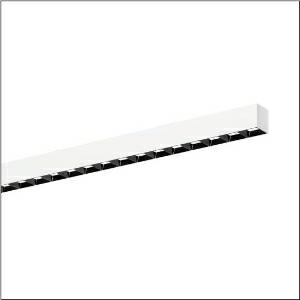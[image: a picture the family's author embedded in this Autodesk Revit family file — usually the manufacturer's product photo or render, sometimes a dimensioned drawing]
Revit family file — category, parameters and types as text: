
# Revit family: silica_r__21_51mx22tat4w_9510
name_source: partatom
category: Lighting Fixtures
units: mm (PartAtom-declared; Revit-internal decimal feet)

## family parameters
Cut with Voids When Loaded = No
Host = Face
Light Source = No
Part Type = Normal
Room Calculation Point = No
Round Connector Dimension = Use Diameter
Shared = No

## types (1)
- --- (1 x LED, 3720 lm, 32.1 W, 6500K)
    Apparent Load = 32 VA
    CIE Flux Codes = 84 100 100 100 100
    Color Rendering = 80
    Color Temperature = 6500K
    Default Elevation = 1800 mm
    Description = Silica® 21, office luminaire, primary light control with darklight reflector, of PMMA, black, CAT 2 (L<= 3000cd/m²), light emission: direct distribution, primary light characteristic: symmetric, installation type: surface-mounted, LED, rated luminous flux: 3.720lm, luminous efficacy: 110lm/W, light colour: 8tw, colour temperature: 2700..6500K, control gear: DALI DT8, with terminal, 3+2-pole, max. 2.5mm², mains connection: 220..240V, AC, 50/60Hz, rated input power: 33.8W, luminaire housing, of aluminium, traffic white (RAL 9016), length: 1.204mm, width: 53mm, height: 53mm, protection rating (complete): IP20, insulation class (complete): insulation class I (protective earthing), certification: CE, permissible operating ambient temperature: 0..+35°C, standard: EN 50419, packaging unit: 1 piece
    Height = 53 mm
    Lamp = 1 x LED
    Lamp Light Flux = 3720 lm
    Lamp Power = 32.1 W
    Lamp count = 1
    Length = 1204 mm
    Luminous efficacy = 116 lm/W
    Manufacturer = Siteco
    ModVariant = No
    Model = 51MX22TAT4W
    Mounting Place = Ceiling
    Mounting Type = Surface mounted
    Number of Poles = 1
    OnlyDefault = Yes
    Power Factor = 1
    Product Name = Silica® 21
    Product group = office luminaire | ceiling mounted
    ProductGroupID = 303
    Protection Class = Protection class I
    Protection Degree = IP 20
    RLX_Detail_Level = 1
    RLX_Emergency_Light_Flux = 0 lm
    RLX_Emergency_Type = 0
    RLX_Emergency_Type_DB = No
    RlxData = <blob elided: 37913 chars, md5=833e0089>
    Socket = socket
    Standby Power = 0 W
    System Light Flux = 3720 lm
    System Power = 32 W
    Type Comments = individual setting
    Type Image = l_1335873.jpg
    URL = http://relux.com
    VarID = @adj_161639
    Voltage = 0 V
    Weight = 0.00 kg
    Width = 53 mm

## geometry (parser evidence)
native form markers: Blend x4, Sweep x9
no freeform markers — native parametric forms only
